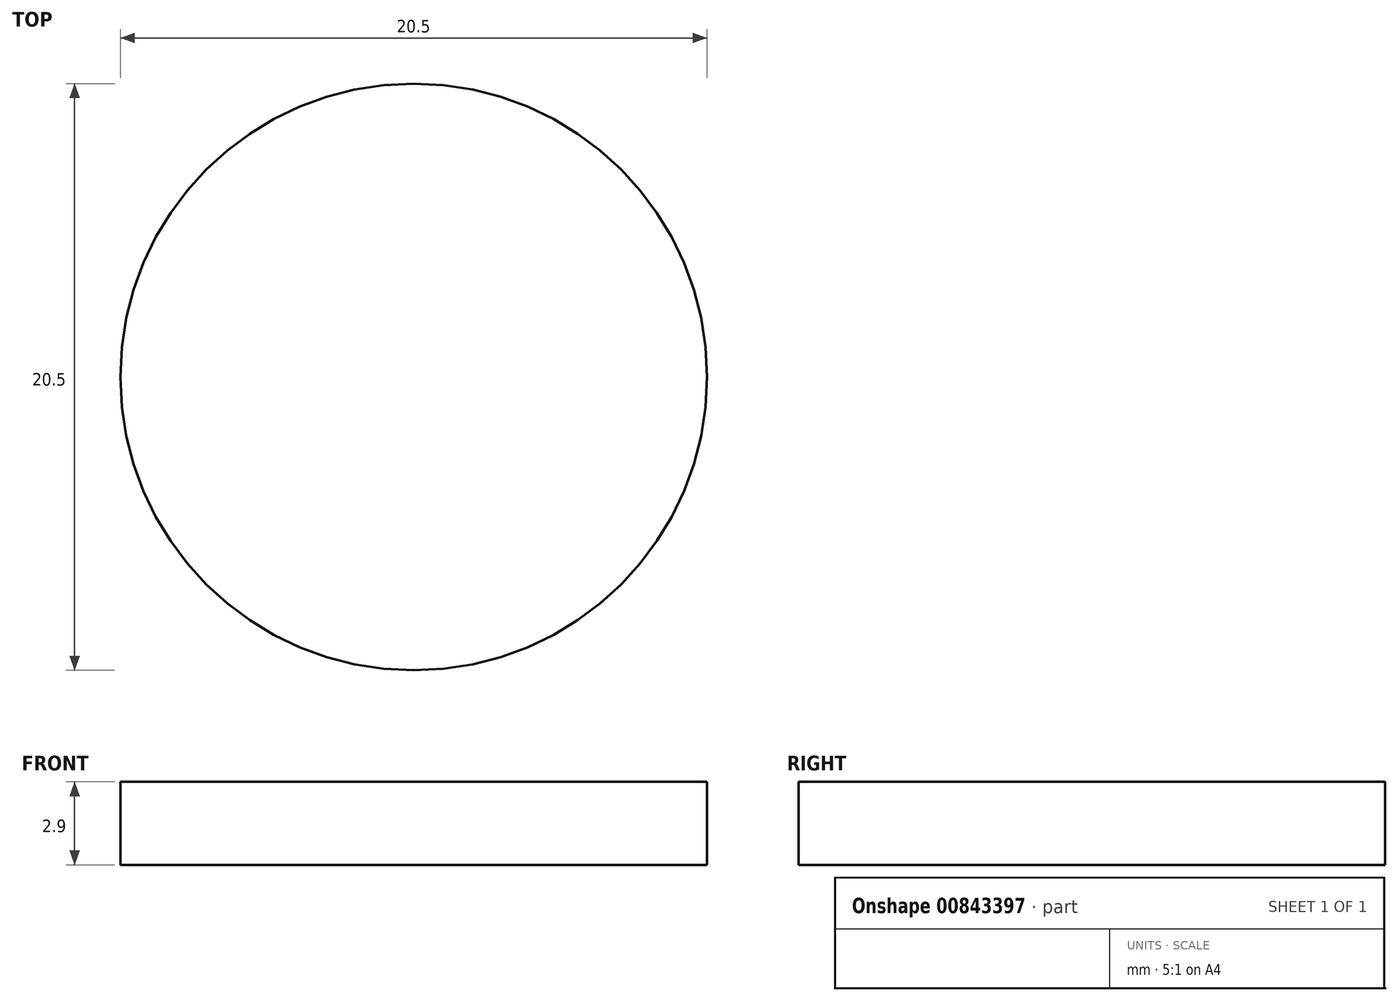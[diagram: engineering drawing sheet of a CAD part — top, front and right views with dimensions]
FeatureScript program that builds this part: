
annotation { "Feature Type Name" : "Feature", "Feature Type Description" : "" }
export const myFeature = defineFeature(function(context is Context, id is Id, definition is map)
    precondition{}
    {
        {
            var Q0;
            Q0=qCreatedBy(makeId("Top.planeOp"),FACE);
            var sketch = newSketch(context, id + "F0", { "sketchPlane" : qUnion([Q0])});
            skCircle(sketch, "E0", {"center": v(0, 0) * mm, "radius": 10.25 * mm});
            skSolve(sketch);
        }
        {
            var Q0;
            Q0 = qSketchRegion(id + "F0", true);
            extrude(context, id + "F1", {"entities" : qUnion([Q0]), "depth" : 2.9 * mm, "offsetDistance" : 25 * mm});
        }
    });
